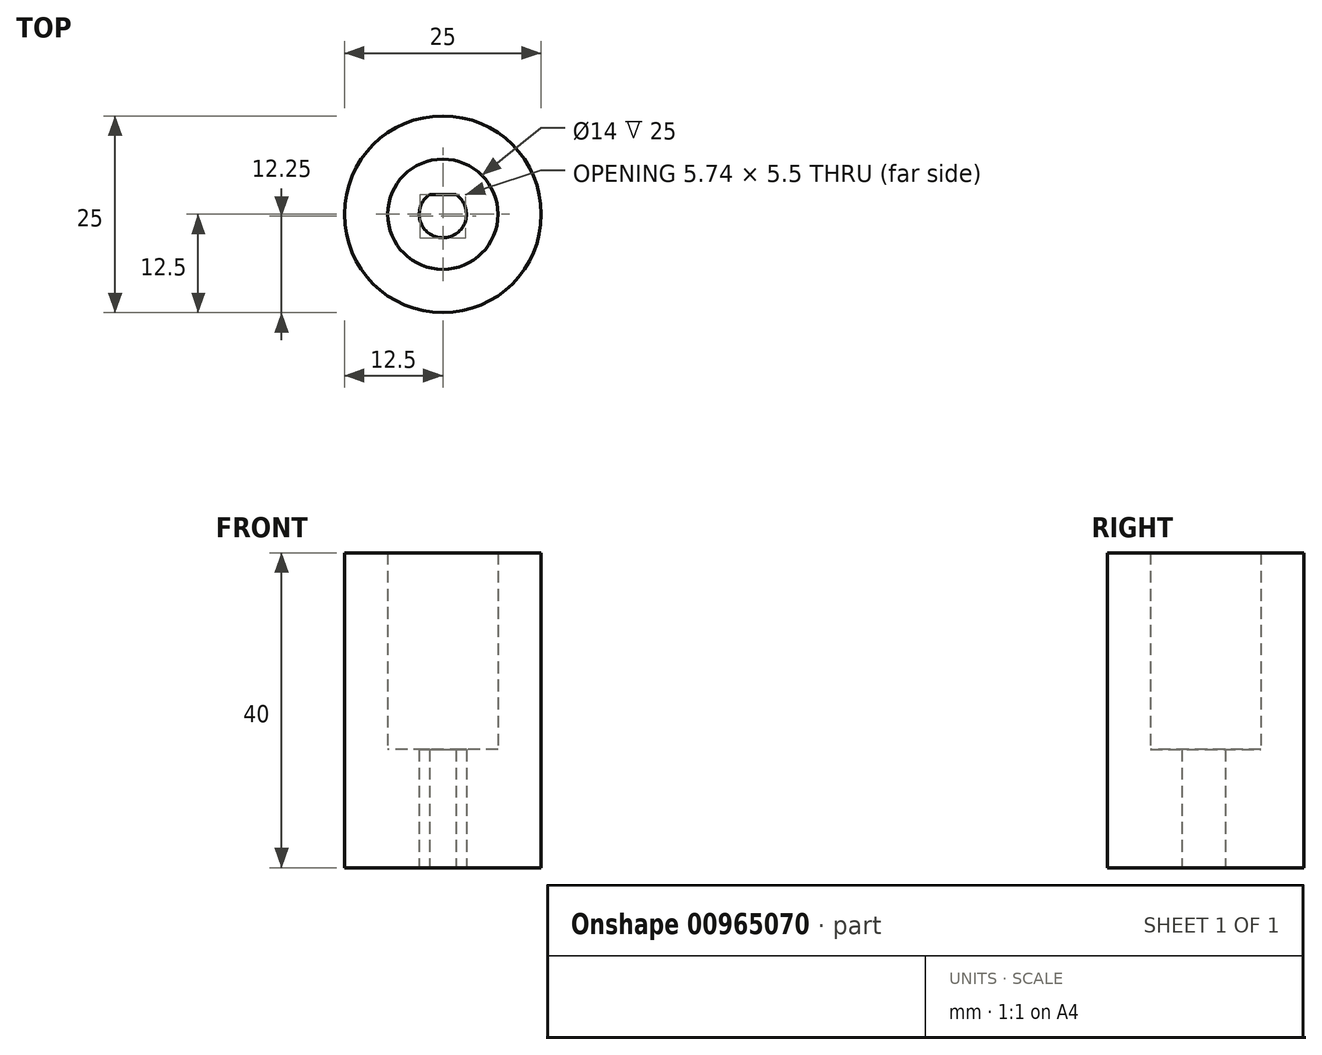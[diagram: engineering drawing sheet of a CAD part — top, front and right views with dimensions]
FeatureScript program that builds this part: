
annotation { "Feature Type Name" : "Feature", "Feature Type Description" : "" }
export const myFeature = defineFeature(function(context is Context, id is Id, definition is map)
    precondition{}
    {
        {
            var Q0;
            Q0=qCreatedBy(makeId("Top.planeOp"),FACE);
            var sketch = newSketch(context, id + "F0", { "sketchPlane" : qUnion([Q0])});
            skCircle(sketch, "E0", {"center": v(0, 0) * mm, "radius": 12.5 * mm});
            skCircle(sketch, "E1", {"center": v(0, 0) * mm, "radius": 7 * mm});
            skCircle(sketch, "E2", {"center": v(0, 0) * mm, "radius": 3 * mm});
            skLineSegment(sketch, "E3", {"start": v(-1.66, 2.5) * mm, "end": v(1.66, 2.5) * mm});
            skSolve(sketch);
        }
        {
            var Q0;
            Q0=makeQuery(id+"F0.imprint","IMPRINT",FACE,{"disambiguationData":[TD([[makeQuery(id+"F0.imprint","IMPRINT",EDGE,{"derivedFrom":sQuery(id+"F0.wireOp",EDGE,"E0")}),1.0]])]});
            extrude(context, id + "F1", {"entities" : qUnion([Q0]), "depth" : 40 * mm, "offsetDistance" : 25 * mm});
        }
        {
            var Q0;
            Q0=makeQuery(id+"F0.imprint","IMPRINT",FACE,{"disambiguationData":[TD([[makeQuery(id+"F0.imprint","IMPRINT",EDGE,{"derivedFrom":sQuery(id+"F0.wireOp",EDGE,"E1")}),1.0]])]});
            var Q1;
            {var subQ0=sQuery(id+"F0.wireOp",EDGE,"E3");Q1=makeQuery(id+"F0.imprint","IMPRINT",FACE,{"disambiguationData":[TD([[makeQuery(id+"F0.imprint","IMPRINT",EDGE,{"derivedFrom":subQ0}),1.0]])]});}
            extrude(context, id + "F2", {"entities" : qUnion([Q0, Q1]), "operationType" : NewBodyOperationType.ADD, "depth" : 15 * mm, "offsetDistance" : 25 * mm});
        }
    });
